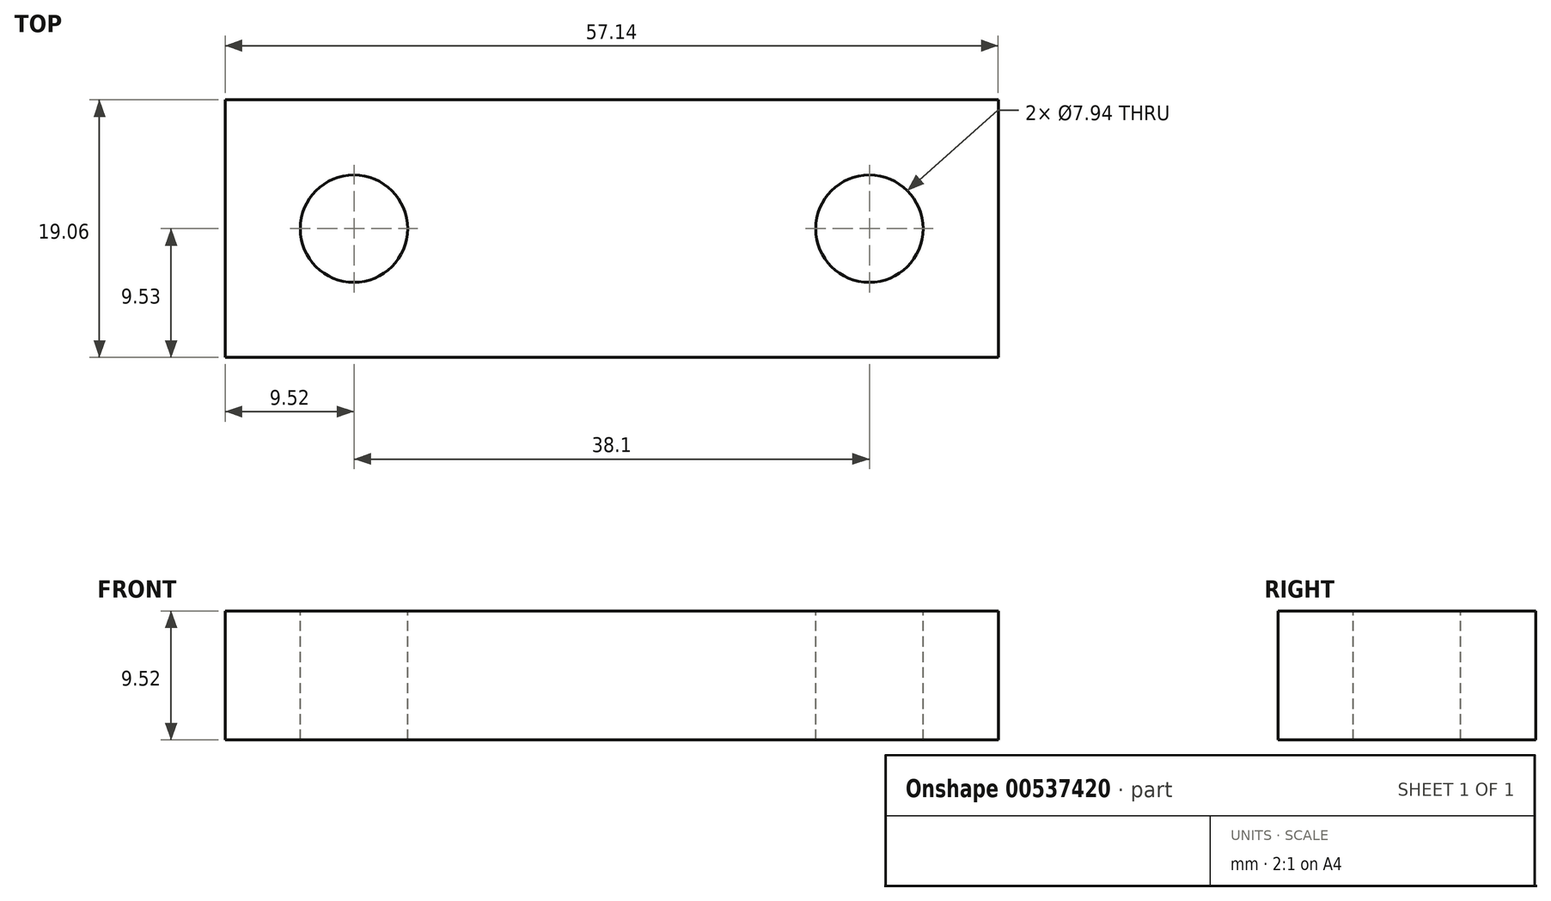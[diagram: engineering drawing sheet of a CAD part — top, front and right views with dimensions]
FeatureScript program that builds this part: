
annotation { "Feature Type Name" : "Feature", "Feature Type Description" : "" }
export const myFeature = defineFeature(function(context is Context, id is Id, definition is map)
    precondition{}
    {
        {
            var Q0;
            Q0=qCreatedBy(makeId("Front.planeOp"),FACE);
            var sketch = newSketch(context, id + "F0", { "sketchPlane" : qUnion([Q0])});
            skLineSegment(sketch, "E0.bottom", {"start": v(28.58, 4.76) * mm, "end": v(-28.58, 4.76) * mm});
            skLineSegment(sketch, "E0.top", {"start": v(28.58, -4.76) * mm, "end": v(-28.58, -4.76) * mm});
            skLineSegment(sketch, "E0.left", {"start": v(28.58, 4.76) * mm, "end": v(28.58, -4.76) * mm});
            skLineSegment(sketch, "E0.right", {"start": v(-28.58, 4.76) * mm, "end": v(-28.58, -4.76) * mm});
            skPoint(sketch, "E0.middle", {"position": v(0, 0) * mm});
            skSolve(sketch);
        }
        {
            var Q0;
            Q0=makeQuery(id+"F0.imprint","IMPRINT",FACE,{"disambiguationData":[TD([[makeQuery(id+"F0.imprint","IMPRINT",EDGE,{"derivedFrom":sQuery(id+"F0.wireOp",EDGE,"E0.bottom")}),1.0]])]});
            extrude(context, id + "F1", {"entities" : qUnion([Q0]), "endBound" : BoundingType.SYMMETRIC, "depth" : 19.05 * mm, "offsetDistance" : 25.4 * mm});
        }
        {
            var Q0;
            Q0=makeQuery(id+"F1.opExtrude","SWEPT_FACE",FACE,{"disambiguationData":[OSD([sQuery(id+"F0.wireOp",EDGE,"E0.bottom")])]});
            var sketch = newSketch(context, id + "F2", { "sketchPlane" : qUnion([Q0])});
            skPoint(sketch, "E1", {"position": v(19.05, 0) * mm});
            skPoint(sketch, "E2.1.0.0", {"position": v(-19.05, 0) * mm});
            skLineSegment(sketch, "E2.direction1", {"start": v(19.05, 0) * mm, "end": v(-19.05, 0) * mm, "construction": true});
            skSolve(sketch);
        }
        {
            var Q0;
            Q0=sQuery(id+"F2.wireOp",VERTEX,"E1");
            var Q1;
            Q1=sQuery(id+"F2.wireOp",VERTEX,"E2.1.0.0");
            var Q2;
            Q2=makeQuery(id+"F1.opExtrude","SWEPT_BODY",BODY,{"disambiguationData":[OSD([sQuery(id+"F0.wireOp",EDGE,"E0.bottom"),sQuery(id+"F0.wireOp",EDGE,"E0.top"),sQuery(id+"F0.wireOp",EDGE,"E0.left"),sQuery(id+"F0.wireOp",EDGE,"E0.right")])]});
            hole(context, id + "F3", {"style" : HoleStyle.SIMPLE, "endStyle" : HoleEndStyle.THROUGH, "standardTappedOrClearance" : lookupTablePath({ "standard" : "ANSI", "fit" : "Normal (ASME)", "engagement" : "75%", "pitch" : "16 tpi", "size" : "3/8", "type" : "Tapped" }), "standardBlindInLast" : lookupTablePath({ "fit" : "Free", "standard" : "ANSI", "engagement" : "75%", "pitch" : "16 tpi", "size" : "3/8", "type" : "Tapped" }), "holeDiameter" : 7.94 * mm, "showTappedDepth" : true, "isTappedThrough" : true, "tappedDepth" : 12.7 * mm, "tapClearance" : 3, "locations" : qUnion([Q0, Q1]), "scope" : qUnion([Q2]), "majorDiameter" : 9.53 * mm});
        }
    });
